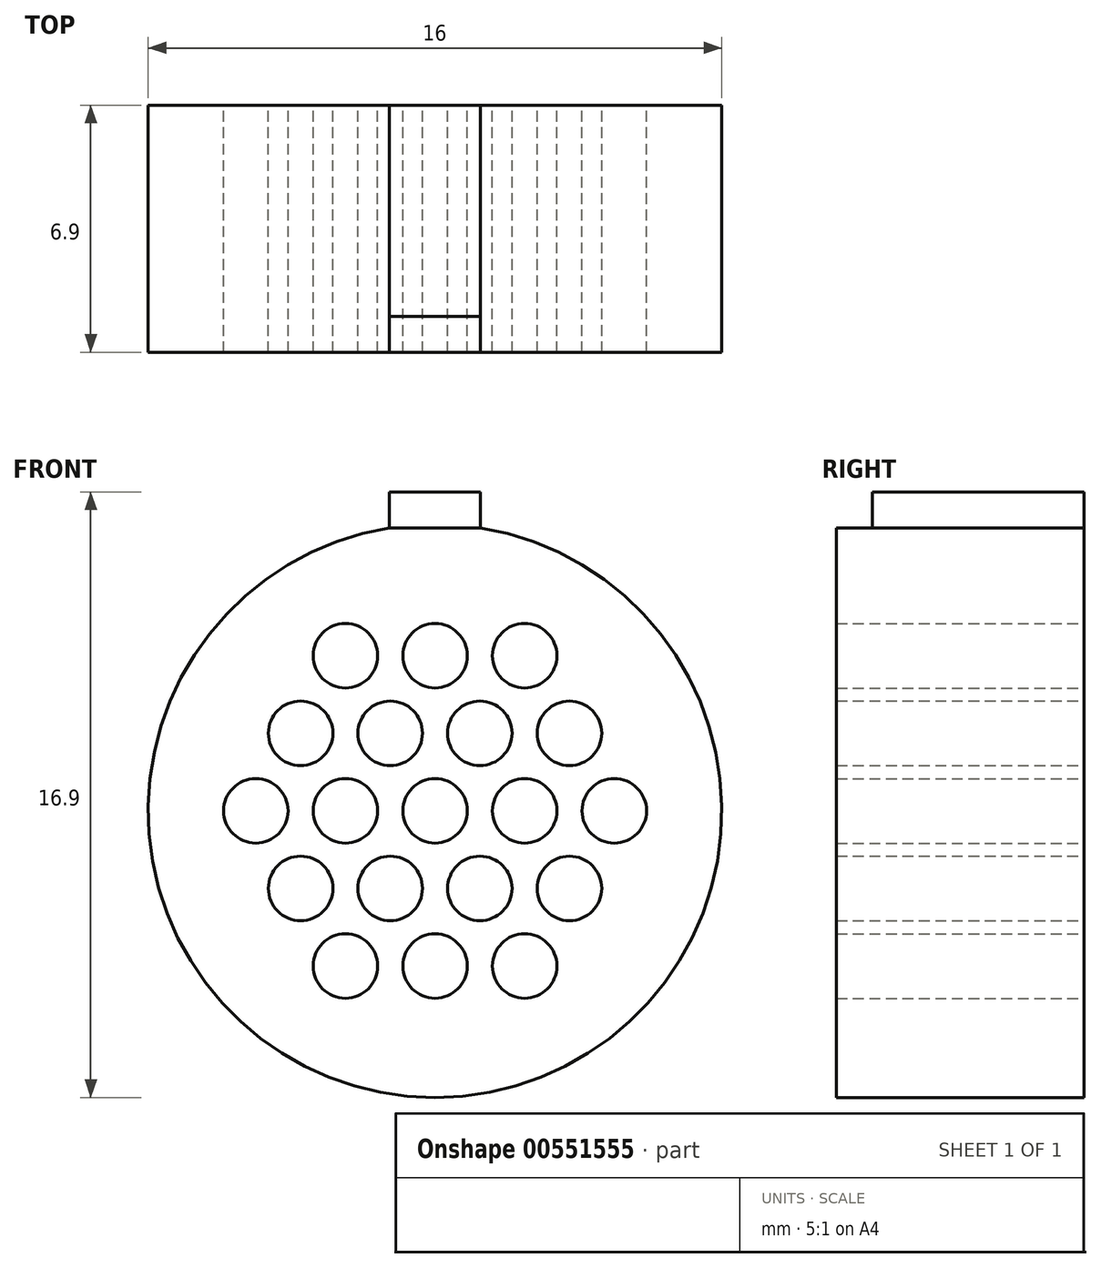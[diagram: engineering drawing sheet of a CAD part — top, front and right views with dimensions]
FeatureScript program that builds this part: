
annotation { "Feature Type Name" : "Feature", "Feature Type Description" : "" }
export const myFeature = defineFeature(function(context is Context, id is Id, definition is map)
    precondition{}
    {
        {
            var Q0;
            Q0=qCreatedBy(makeId("Front.planeOp"),FACE);
            var sketch = newSketch(context, id + "F0", { "sketchPlane" : qUnion([Q0])});
            skCircle(sketch, "E0", {"center": v(0, 0) * mm, "radius": 0.9 * mm});
            skCircle(sketch, "E1", {"center": v(-2.5, 0) * mm, "radius": 0.9 * mm});
            skCircle(sketch, "E2", {"center": v(2.5, 0) * mm, "radius": 0.9 * mm});
            skCircle(sketch, "E3", {"center": v(-5, 0) * mm, "radius": 0.9 * mm});
            skCircle(sketch, "E4", {"center": v(5, 0) * mm, "radius": 0.9 * mm});
            skCircle(sketch, "E5", {"center": v(-1.25, 2.17) * mm, "radius": 0.9 * mm});
            skCircle(sketch, "E6", {"center": v(-3.75, 2.17) * mm, "radius": 0.9 * mm});
            skCircle(sketch, "E7", {"center": v(1.25, 2.17) * mm, "radius": 0.9 * mm});
            skCircle(sketch, "E8", {"center": v(3.75, 2.17) * mm, "radius": 0.9 * mm});
            skCircle(sketch, "E9", {"center": v(-3.75, -2.17) * mm, "radius": 0.9 * mm});
            skCircle(sketch, "E10", {"center": v(-1.25, -2.17) * mm, "radius": 0.9 * mm});
            skCircle(sketch, "E11", {"center": v(1.25, -2.17) * mm, "radius": 0.9 * mm});
            skCircle(sketch, "E12", {"center": v(3.75, -2.17) * mm, "radius": 0.9 * mm});
            skCircle(sketch, "E13", {"center": v(-2.5, 4.33) * mm, "radius": 0.9 * mm});
            skCircle(sketch, "E14", {"center": v(0, 4.33) * mm, "radius": 0.9 * mm});
            skCircle(sketch, "E15", {"center": v(2.5, 4.33) * mm, "radius": 0.9 * mm});
            skCircle(sketch, "E16", {"center": v(-2.5, -4.33) * mm, "radius": 0.9 * mm});
            skCircle(sketch, "E17", {"center": v(0, -4.33) * mm, "radius": 0.9 * mm});
            skCircle(sketch, "E18", {"center": v(2.5, -4.33) * mm, "radius": 0.9 * mm});
            skArc(sketch, "E19", {"start": v(-1.27, 7.9) * mm, "mid": v(0, -8) * mm, "end": v(1.27, 7.9) * mm});
            skLineSegment(sketch, "E20.bottom", {"start": v(1.27, 8.9) * mm, "end": v(-1.27, 8.9) * mm});
            skLineSegment(sketch, "E20.left", {"start": v(1.27, 8.9) * mm, "end": v(1.27, 7.9) * mm});
            skLineSegment(sketch, "E20.right", {"start": v(-1.27, 8.9) * mm, "end": v(-1.27, 7.9) * mm});
            skPoint(sketch, "E20.middle", {"position": v(0, 8) * mm});
            skPoint(sketch, "E21.orphan", {"position": v(-1.27, 7.1) * mm});
            skPoint(sketch, "E22.orphan", {"position": v(1.27, 7.1) * mm});
            skSolve(sketch);
        }
        {
            var Q0;
            Q0 = qSketchRegion(id + "F0", true);
            extrude(context, id + "F1", {"entities" : qUnion([Q0]), "depth" : 6.9 * mm, "offsetDistance" : 25 * mm});
        }
        {
            var Q0;
            Q0=makeQuery(id+"F1.opExtrude","SWEPT_FACE",FACE,{"disambiguationData":[OSD([sQuery(id+"F0.wireOp",EDGE,"E20.right")])]});
            var sketch = newSketch(context, id + "F2", { "sketchPlane" : qUnion([Q0])});
            skLineSegment(sketch, "E23.bottom", {"start": v(6.9, 8.9) * mm, "end": v(5.9, 8.9) * mm});
            skLineSegment(sketch, "E23.top", {"start": v(6.9, 7.9) * mm, "end": v(5.9, 7.9) * mm});
            skLineSegment(sketch, "E23.left", {"start": v(6.9, 8.9) * mm, "end": v(6.9, 7.9) * mm});
            skLineSegment(sketch, "E23.right", {"start": v(5.9, 8.9) * mm, "end": v(5.9, 7.9) * mm});
            skSolve(sketch);
        }
        {
            var Q0;
            Q0 = qSketchRegion(id + "F2", true);
            extrude(context, id + "F3", {"entities" : qUnion([Q0]), "operationType" : NewBodyOperationType.REMOVE, "oppositeDirection" : true, "depth" : 2.54 * mm, "offsetDistance" : 25 * mm});
        }
    });
